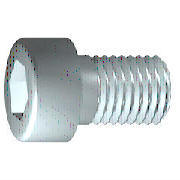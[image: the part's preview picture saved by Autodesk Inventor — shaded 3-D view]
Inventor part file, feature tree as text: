
AUTODESK INVENTOR PART (.ipt)
format: ipt  version: 2016 (Build 200138000, 138)  size: 198,144 bytes
history: native  units: mm (DEFAULTED — no unit token found)
features: sketch x2, extrude x1, plane x1, fillet x1
ambient origin geometry x7: Origin, YZ Plane, XY Plane, X Axis, Y Axis, Z Axis, Center Point
bodies: Solid1 (feature_tree), Body (feature_tree)
feature tree (5):
  extrude  "Slot"  Depth=4.0mm
  plane  "Work Plane1"
  fillet  "Fillet2"  Radius=4.0mm
  sketch  "Sketch1"  dims[d1=8.25mm d2=0.429515mm d3=4.0mm]
  sketch  "Sketch2"  dims[d4=2.0mm d5=60.0deg d6=4.0mm d7=4.0mm d8=3.464102mm d9=7.0mm d10=90.0deg d11=10.0mm d12=0.0mm d13=8.25mm d14=0.0mm d15=0.429415mm d16=0.429415mm d17=0.4mm d19=0.0mm d26=10.0mm d27=45.0deg d28=0.0mm d29=0.0mm d30=0.1mm]
